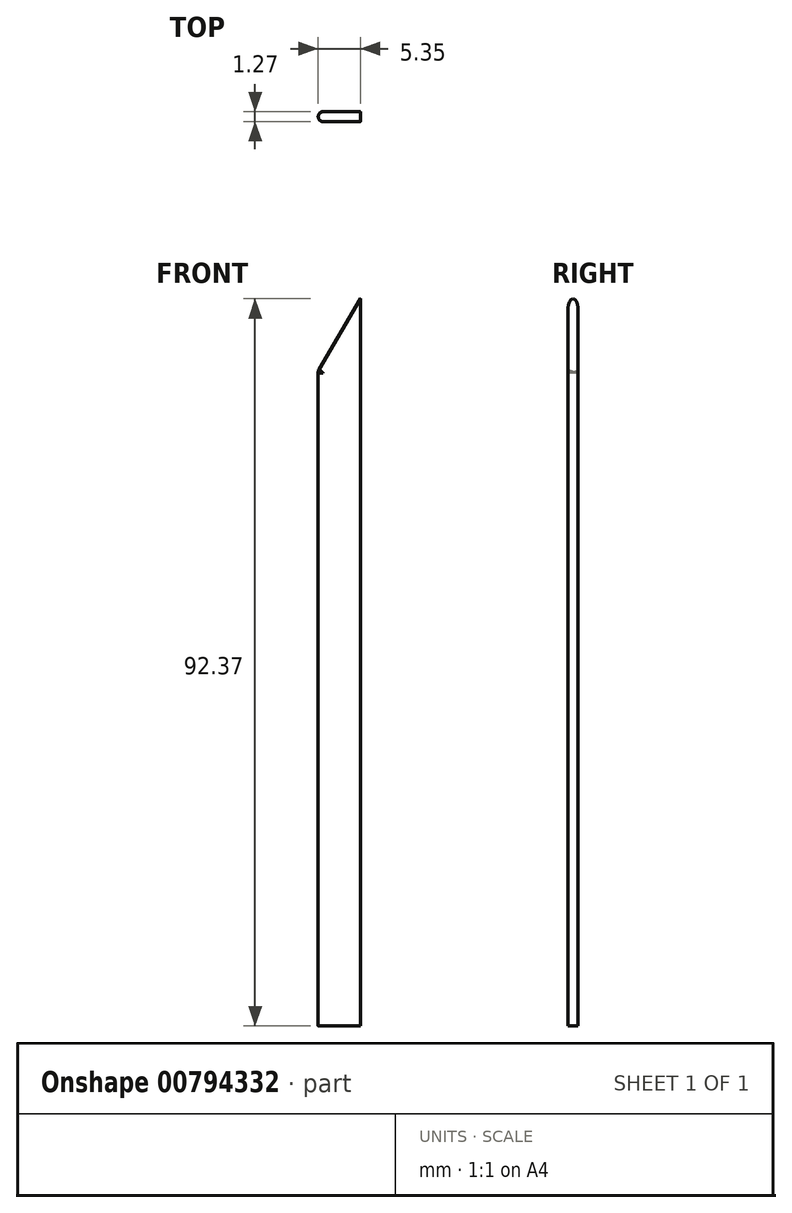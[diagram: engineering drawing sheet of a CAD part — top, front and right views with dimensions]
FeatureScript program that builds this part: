
annotation { "Feature Type Name" : "Feature", "Feature Type Description" : "" }
export const myFeature = defineFeature(function(context is Context, id is Id, definition is map)
    precondition{}
    {
        {
            var Q0;
            Q0=qCreatedBy(makeId("Front.planeOp"),FACE);
            var sketch = newSketch(context, id + "F0", { "sketchPlane" : qUnion([Q0])});
            skLineSegment(sketch, "E0", {"start": v(18.08, 69.7) * mm, "end": v(18.08, -22.77) * mm});
            skLineSegment(sketch, "E1", {"start": v(18.08, -22.77) * mm, "end": v(12.73, -22.77) * mm});
            skLineSegment(sketch, "E2", {"start": v(12.73, -22.77) * mm, "end": v(12.73, 60.6) * mm});
            skLineSegment(sketch, "E3", {"start": v(12.73, 60.6) * mm, "end": v(18.08, 69.7) * mm});
            skSolve(sketch);
        }
        {
            var Q0;
            Q0=makeQuery(id+"F0.imprint","IMPRINT",FACE,{"disambiguationData":[TD([[makeQuery(id+"F0.imprint","IMPRINT",EDGE,{"derivedFrom":sQuery(id+"F0.wireOp",EDGE,"E0")}),-1.0]])]});
            extrude(context, id + "F1", {"entities" : qUnion([Q0]), "depth" : 1.27 * mm, "offsetDistance" : 25.4 * mm});
        }
        {
            var Q0;
            Q0=makeQuery(id+"F1.opExtrude","CAP_EDGE",EDGE,{"disambiguationData":[OSD([sQuery(id+"F0.wireOp",EDGE,"E3")])],"isStart":false});
            fillet(context, id + "F2", {"entities" : qUnion([Q0]), "radius" : 0.74 * mm, "tangentPropagation" : true, "allowEdgeOverflow" : false});
        }
        {
            var Q0;
            Q0=makeQuery(id+"F1.opExtrude","CAP_EDGE",EDGE,{"disambiguationData":[OSD([sQuery(id+"F0.wireOp",EDGE,"E3")])],"isStart":true});
            fillet(context, id + "F3", {"entities" : qUnion([Q0]), "radius" : 0.8 * mm, "tangentPropagation" : true, "allowEdgeOverflow" : false});
        }
        {
            var Q0;
            Q0=makeQuery(id+"F1.opExtrude","CAP_EDGE",EDGE,{"disambiguationData":[OSD([sQuery(id+"F0.wireOp",EDGE,"E2")])],"isStart":true});
            fillet(context, id + "F4", {"entities" : qUnion([Q0]), "radius" : 0.61 * mm, "tangentPropagation" : true, "allowEdgeOverflow" : false});
        }
        {
            var Q0;
            Q0=makeQuery(id+"F1.opExtrude","CAP_EDGE",EDGE,{"disambiguationData":[OSD([sQuery(id+"F0.wireOp",EDGE,"E2")])],"isStart":false});
            fillet(context, id + "F5", {"entities" : qUnion([Q0]), "radius" : 0.61 * mm, "tangentPropagation" : true, "allowEdgeOverflow" : false});
        }
    });
